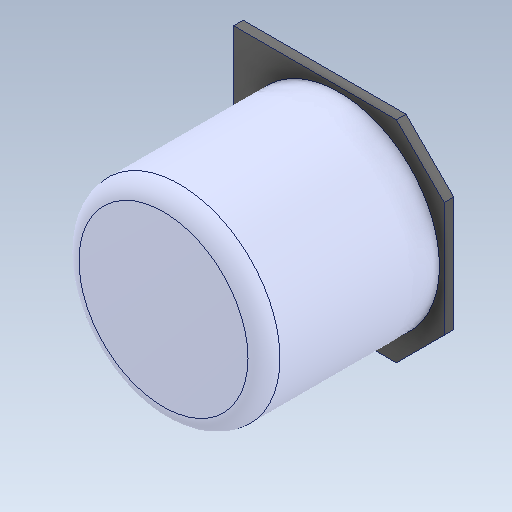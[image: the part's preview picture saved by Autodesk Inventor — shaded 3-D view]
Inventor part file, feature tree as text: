
AUTODESK INVENTOR PART (.ipt)
format: ipt  version: 2021 (Build 250183000, 183)  size: 136,704 bytes
history: native  units: in
note: dims shown in document units (in); Inventor stores cm internally (conversion verified against a paired STEP export)
features: fillet x1
ambient origin geometry x8: Origin, YZ Plane, XZ Plane, XY Plane, X Axis, Y Axis, Z Axis, Center Point
bodies: Solid1 (feature_tree)
feature tree (1):
  fillet  "Fillet1"  [1 undecoded]
note: 1 required parameter value undecoded (feature->parameter linkage not recoverable at this tier; creation-order binding heuristic only, values carry confidence <= 0.55)
